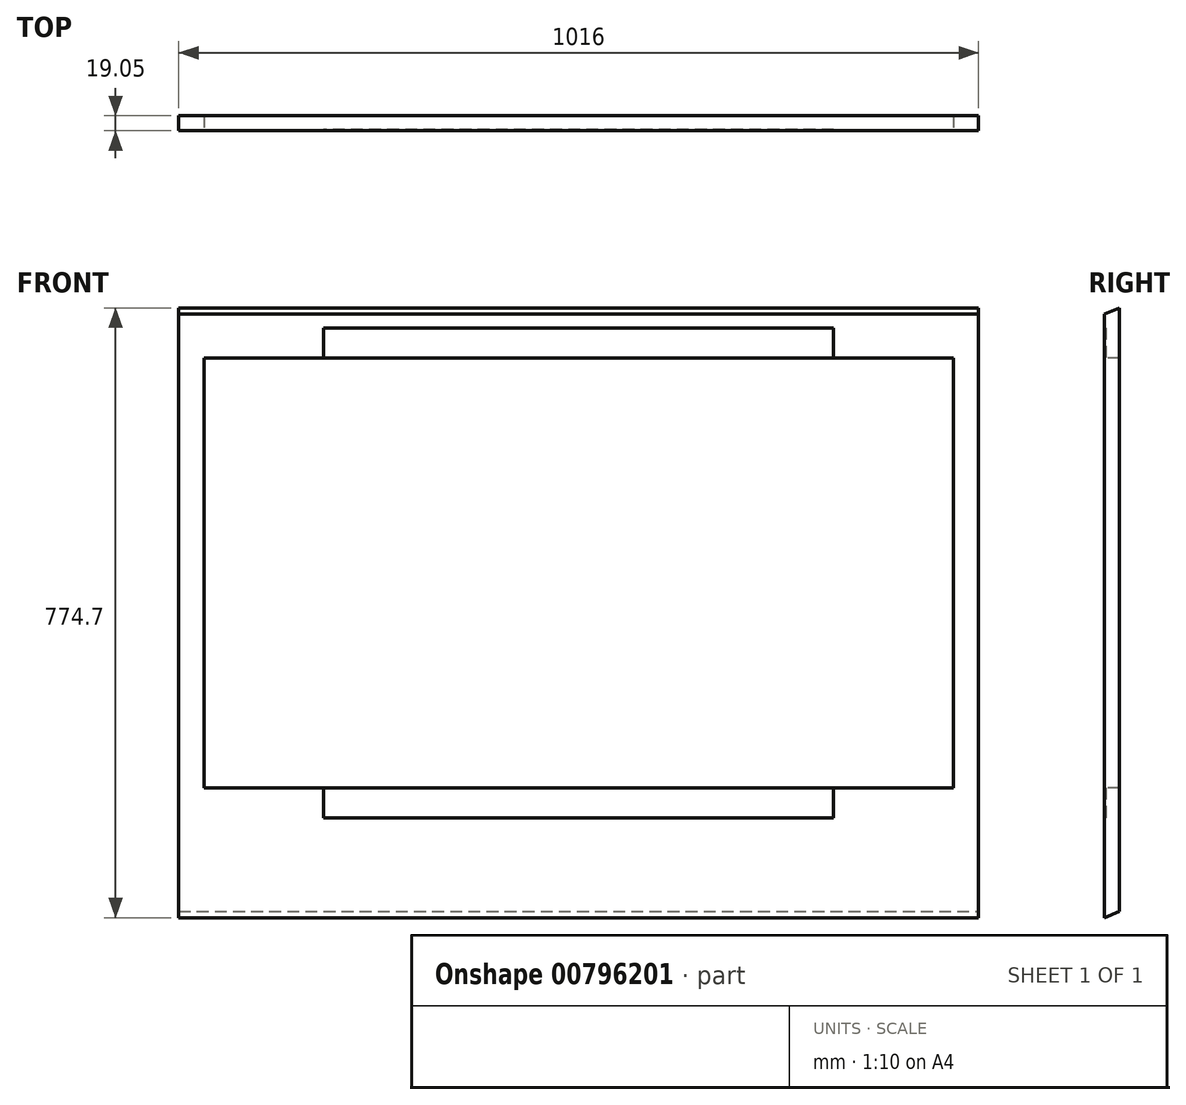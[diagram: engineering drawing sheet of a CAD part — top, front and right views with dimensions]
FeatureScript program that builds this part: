
annotation { "Feature Type Name" : "Feature", "Feature Type Description" : "" }
export const myFeature = defineFeature(function(context is Context, id is Id, definition is map)
    precondition{}
    {
        {
            var Q0;
            Q0=qCreatedBy(makeId("Front.planeOp"),FACE);
            var sketch = newSketch(context, id + "F0", { "sketchPlane" : qUnion([Q0])});
            skLineSegment(sketch, "E0.bottom", {"start": v(-554.86, 497.72) * mm, "end": v(461.14, 497.72) * mm});
            skLineSegment(sketch, "E0.top", {"start": v(-554.86, -276.98) * mm, "end": v(461.14, -276.98) * mm});
            skLineSegment(sketch, "E0.left", {"start": v(-554.86, 497.72) * mm, "end": v(-554.86, -276.98) * mm});
            skLineSegment(sketch, "E0.right", {"start": v(461.14, 497.72) * mm, "end": v(461.14, -276.98) * mm});
            skSolve(sketch);
        }
        {
            var Q0;
            Q0=makeQuery(id+"F0.imprint","IMPRINT",FACE,{"disambiguationData":[TD([[makeQuery(id+"F0.imprint","IMPRINT",EDGE,{"derivedFrom":sQuery(id+"F0.wireOp",EDGE,"E0.bottom")}),-1.0]])]});
            extrude(context, id + "F1", {"entities" : qUnion([Q0]), "oppositeDirection" : true, "depth" : 19.05 * mm, "offsetDistance" : 25.4 * mm});
        }
        {
            var Q0;
            Q0=makeQuery(id+"F1.opExtrude","SWEPT_FACE",FACE,{"disambiguationData":[OSD([sQuery(id+"F0.wireOp",EDGE,"E0.right")])]});
            var sketch = newSketch(context, id + "F2", { "sketchPlane" : qUnion([Q0])});
            skLineSegment(sketch, "E1", {"start": v(0, -276.98) * mm, "end": v(19.05, -276.98) * mm});
            skLineSegment(sketch, "E2", {"start": v(0, -276.98) * mm, "end": v(19.05, -269.09) * mm});
            skLineSegment(sketch, "E3", {"start": v(19.05, -269.09) * mm, "end": v(19.05, -276.98) * mm});
            skSolve(sketch);
        }
        {
            var Q0;
            Q0=makeQuery(id+"F2.imprint","IMPRINT",FACE,{"disambiguationData":[TD([[makeQuery(id+"F2.imprint","IMPRINT",EDGE,{"derivedFrom":sQuery(id+"F2.wireOp",EDGE,"E1")}),-1.0]])]});
            extrude(context, id + "F3", {"entities" : qUnion([Q0]), "operationType" : NewBodyOperationType.REMOVE, "endBound" : BoundingType.THROUGH_ALL, "oppositeDirection" : true, "depth" : 25.4 * mm, "offsetDistance" : 25.4 * mm});
        }
        {
            var Q0;
            Q0=makeQuery(id+"F1.opExtrude","CAP_FACE",FACE,{"disambiguationData":[OSD([sQuery(id+"F0.wireOp",EDGE,"E0.bottom"),sQuery(id+"F0.wireOp",EDGE,"E0.top"),sQuery(id+"F0.wireOp",EDGE,"E0.left"),sQuery(id+"F0.wireOp",EDGE,"E0.right")])],"isStart":true});
            var sketch = newSketch(context, id + "F4", { "sketchPlane" : qUnion([Q0])});
            skLineSegment(sketch, "E4.bottom", {"start": v(-522.95, 433.9) * mm, "end": v(429.24, 433.9) * mm});
            skLineSegment(sketch, "E4.top", {"start": v(-522.95, -111.9) * mm, "end": v(429.24, -111.9) * mm});
            skLineSegment(sketch, "E4.left", {"start": v(-522.95, 433.9) * mm, "end": v(-522.95, -111.9) * mm});
            skLineSegment(sketch, "E4.right", {"start": v(429.24, 433.9) * mm, "end": v(429.24, -111.9) * mm});
            skSolve(sketch);
        }
        {
            var Q0;
            Q0=makeQuery(id+"F4.imprint","IMPRINT",FACE,{"disambiguationData":[TD([[makeQuery(id+"F4.imprint","IMPRINT",EDGE,{"derivedFrom":sQuery(id+"F4.wireOp",EDGE,"E4.bottom")}),-1.0]])]});
            extrude(context, id + "F5", {"entities" : qUnion([Q0]), "operationType" : NewBodyOperationType.REMOVE, "endBound" : BoundingType.THROUGH_ALL, "oppositeDirection" : true, "depth" : 25.4 * mm, "offsetDistance" : 25.4 * mm});
        }
        {
            var Q0;
            Q0=makeQuery(id+"F1.opExtrude","CAP_FACE",FACE,{"disambiguationData":[OSD([sQuery(id+"F0.wireOp",EDGE,"E0.bottom"),sQuery(id+"F0.wireOp",EDGE,"E0.top"),sQuery(id+"F0.wireOp",EDGE,"E0.left"),sQuery(id+"F0.wireOp",EDGE,"E0.right")])],"isStart":true});
            var sketch = newSketch(context, id + "F6", { "sketchPlane" : qUnion([Q0])});
            skLineSegment(sketch, "E5", {"start": v(-46.86, 472.32) * mm, "end": v(277, 472.32) * mm});
            skLineSegment(sketch, "E6", {"start": v(277, 472.32) * mm, "end": v(277, 433.9) * mm});
            skLineSegment(sketch, "E7", {"start": v(277, 433.9) * mm, "end": v(-370.7, 433.9) * mm});
            skLineSegment(sketch, "E8", {"start": v(-370.7, 433.9) * mm, "end": v(-370.7, 472.32) * mm});
            skLineSegment(sketch, "E9", {"start": v(-370.7, 472.32) * mm, "end": v(-46.86, 472.32) * mm});
            skLineSegment(sketch, "E10", {"start": v(-522.95, 161) * mm, "end": v(-316.04, 161) * mm});
            skLineSegment(sketch, "E11.MirrorCS", {"start": v(-370.7, -111.9) * mm, "end": v(-370.7, -150.33) * mm});
            skLineSegment(sketch, "E12.MirrorCS", {"start": v(277, -111.9) * mm, "end": v(-370.7, -111.9) * mm});
            skLineSegment(sketch, "E13.MirrorCS", {"start": v(-370.7, -150.33) * mm, "end": v(-46.86, -150.33) * mm});
            skLineSegment(sketch, "E14.MirrorCS", {"start": v(-46.86, -150.33) * mm, "end": v(277, -150.33) * mm});
            skLineSegment(sketch, "E15.MirrorCS", {"start": v(277, -150.33) * mm, "end": v(277, -111.9) * mm});
            skSolve(sketch);
        }
        {
            var Q0;
            Q0=makeQuery(id+"F6.imprint","IMPRINT",FACE,{"disambiguationData":[TD([[makeQuery(id+"F6.imprint","IMPRINT",EDGE,{"derivedFrom":sQuery(id+"F6.wireOp",EDGE,"E5")}),-1.0]])]});
            var Q1;
            Q1=makeQuery(id+"F6.imprint","IMPRINT",FACE,{"disambiguationData":[TD([[makeQuery(id+"F6.imprint","IMPRINT",EDGE,{"derivedFrom":sQuery(id+"F6.wireOp",EDGE,"E11.MirrorCS")}),1.0]])]});
            var Q2;
            {var subQ3=sQuery(id+"F6.wireOp",EDGE,"E7");Q2=makeQuery(id+"F6.imprint","IMPRINT",FACE,{"disambiguationData":[TD([[makeQuery(id+"F6.imprint","IMPRINT",EDGE,{"derivedFrom":subQ3}),-1.0]])]});}
            extrude(context, id + "F7", {"entities" : qUnion([Q0, Q1, Q2]), "operationType" : NewBodyOperationType.REMOVE, "oppositeDirection" : true, "depth" : 1.59 * mm, "offsetDistance" : 25.4 * mm});
        }
        {
            var Q0;
            Q0=makeQuery(id+"F1.opExtrude","SWEPT_FACE",FACE,{"disambiguationData":[OSD([sQuery(id+"F0.wireOp",EDGE,"E0.right")])]});
            var sketch = newSketch(context, id + "F8", { "sketchPlane" : qUnion([Q0])});
            skLineSegment(sketch, "E16", {"start": v(0, 497.72) * mm, "end": v(19.05, 497.72) * mm});
            skLineSegment(sketch, "E17", {"start": v(19.05, 497.72) * mm, "end": v(0, 489.83) * mm});
            skLineSegment(sketch, "E18", {"start": v(0, 489.83) * mm, "end": v(0, 497.72) * mm});
            skSolve(sketch);
        }
        {
            var Q0;
            Q0=makeQuery(id+"F8.imprint","IMPRINT",FACE,{"disambiguationData":[TD([[makeQuery(id+"F8.imprint","IMPRINT",EDGE,{"derivedFrom":sQuery(id+"F8.wireOp",EDGE,"E16")}),1.0]])]});
            extrude(context, id + "F9", {"entities" : qUnion([Q0]), "operationType" : NewBodyOperationType.REMOVE, "endBound" : BoundingType.THROUGH_ALL, "oppositeDirection" : true, "depth" : 25.4 * mm, "offsetDistance" : 25.4 * mm});
        }
    });
